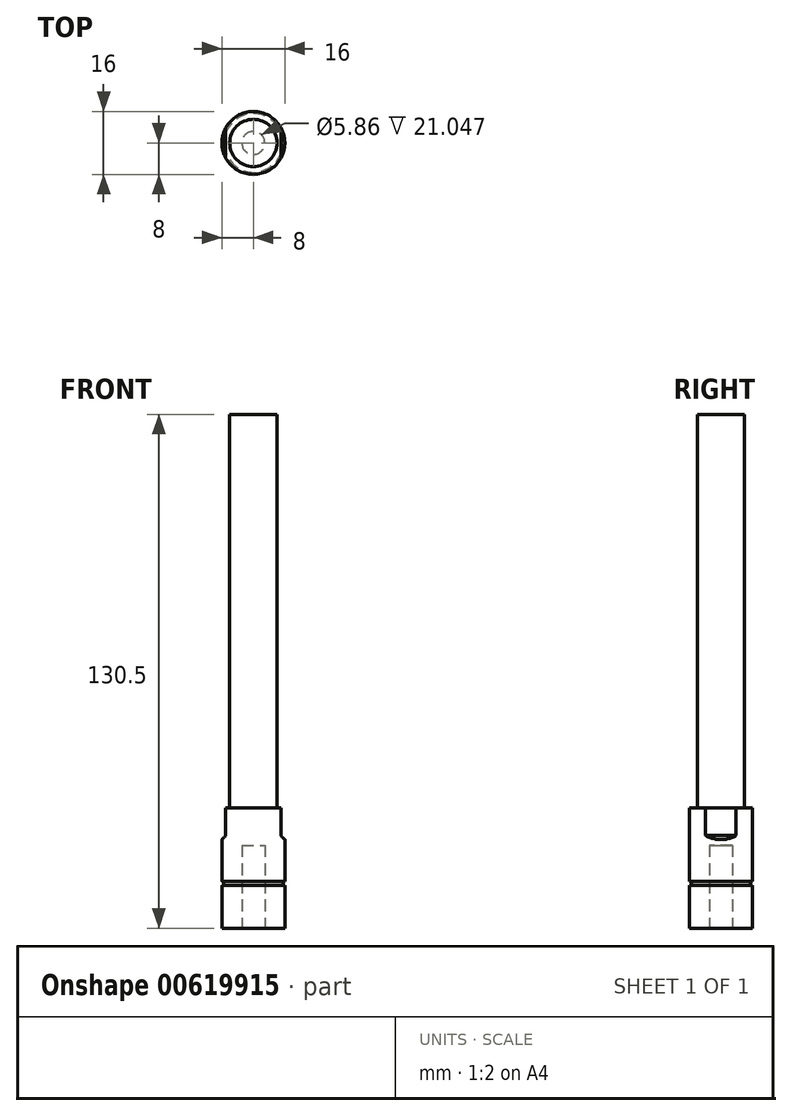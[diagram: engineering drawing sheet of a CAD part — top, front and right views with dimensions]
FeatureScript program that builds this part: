
annotation { "Feature Type Name" : "Feature", "Feature Type Description" : "" }
export const myFeature = defineFeature(function(context is Context, id is Id, definition is map)
    precondition{}
    {
        {
            var Q0;
            Q0=qCreatedBy(makeId("Front.planeOp"),FACE);
            var sketch = newSketch(context, id + "F0", { "sketchPlane" : qUnion([Q0])});
            skLineSegment(sketch, "E0.bottom", {"start": v(2.93, 0) * mm, "end": v(8, 0) * mm});
            skLineSegment(sketch, "E0.top", {"start": v(6, 30.5) * mm, "end": v(8, 30.5) * mm});
            skLineSegment(sketch, "E0.left", {"start": v(0, 21.05) * mm, "end": v(0, 30.5) * mm});
            skLineSegment(sketch, "E0.right", {"start": v(8, 0) * mm, "end": v(8, 10.84) * mm});
            skLineSegment(sketch, "E1.top", {"start": v(0, 130.5) * mm, "end": v(6, 130.5) * mm});
            skLineSegment(sketch, "E1.left", {"start": v(0, 30.5) * mm, "end": v(0, 130.5) * mm});
            skLineSegment(sketch, "E1.right", {"start": v(6, 30.5) * mm, "end": v(6, 130.5) * mm});
            skArc(sketch, "E2", {"start": v(8, 11.84) * mm, "mid": v(7.5, 11.34) * mm, "end": v(8, 10.84) * mm});
            skLineSegment(sketch, "E3.top", {"start": v(0, 21.05) * mm, "end": v(2.93, 21.05) * mm});
            skLineSegment(sketch, "E3.right", {"start": v(2.93, 0) * mm, "end": v(2.93, 21.05) * mm});
            skLineSegment(sketch, "E4.trimOffspring", {"start": v(8, 11.84) * mm, "end": v(8, 30.5) * mm});
            skSolve(sketch);
        }
        {
            var Q0;
            Q0 = qSketchRegion(id + "F0", true);
            var Q1;
            Q1=sQuery(id+"F0.wireOp",EDGE,"E1.left");
            revolve(context, id + "F1", {"entities" : qUnion([Q0]), "axis" : qUnion([Q1]), "revolveType" : RevolveType.FULL});
        }
        {
            var Q0;
            Q0=makeQuery(id+"F1.opRevolve","SWEPT_FACE",FACE,{"disambiguationData":[OSD([sQuery(id+"F0.wireOp",EDGE,"E0.top")])]});
            var sketch = newSketch(context, id + "F2", { "sketchPlane" : qUnion([Q0])});
            skLineSegment(sketch, "E5.bottom", {"start": v(7, -15) * mm, "end": v(-7, -15) * mm});
            skLineSegment(sketch, "E5.top", {"start": v(7, 15) * mm, "end": v(-7, 15) * mm});
            skLineSegment(sketch, "E5.left", {"start": v(7, -15) * mm, "end": v(7, 15) * mm});
            skLineSegment(sketch, "E5.right", {"start": v(-7, -15) * mm, "end": v(-7, 15) * mm});
            skPoint(sketch, "E5.middle", {"position": v(0, 0) * mm});
            skLineSegment(sketch, "E6.bottom", {"start": v(9.8, -18.57) * mm, "end": v(-9.8, -18.57) * mm});
            skLineSegment(sketch, "E6.top", {"start": v(9.8, 18.57) * mm, "end": v(-9.8, 18.57) * mm});
            skLineSegment(sketch, "E6.left", {"start": v(9.8, -18.57) * mm, "end": v(9.8, 18.57) * mm});
            skLineSegment(sketch, "E6.right", {"start": v(-9.8, -18.57) * mm, "end": v(-9.8, 18.57) * mm});
            skSolve(sketch);
        }
        {
            var Q0;
            Q0 = qSketchRegion(id + "F2", true);
            extrude(context, id + "F3", {"entities" : qUnion([Q0]), "operationType" : NewBodyOperationType.REMOVE, "oppositeDirection" : true, "depth" : 8 * mm, "offsetDistance" : 25 * mm});
        }
        {
            var Q0;
            Q0=makeQuery(id+"F3.boolean.opBoolean","COPY",EDGE,{"derivedFrom":makeQuery(id+"F3.opExtrude","CAP_EDGE",EDGE,{"disambiguationData":[OSD([sQuery(id+"F2.wireOp",EDGE,"E5.right")])],"isStart":false})});
            var Q1;
            Q1=makeQuery(id+"F3.boolean.opBoolean","COPY",EDGE,{"derivedFrom":makeQuery(id+"F3.opExtrude","CAP_EDGE",EDGE,{"disambiguationData":[OSD([sQuery(id+"F2.wireOp",EDGE,"E5.left")])],"isStart":false})});
            chamfer(context, id + "F4", {"entities" : qUnion([Q0, Q1]), "width" : 1 * mm, "tangentPropagation" : true});
        }
    });
